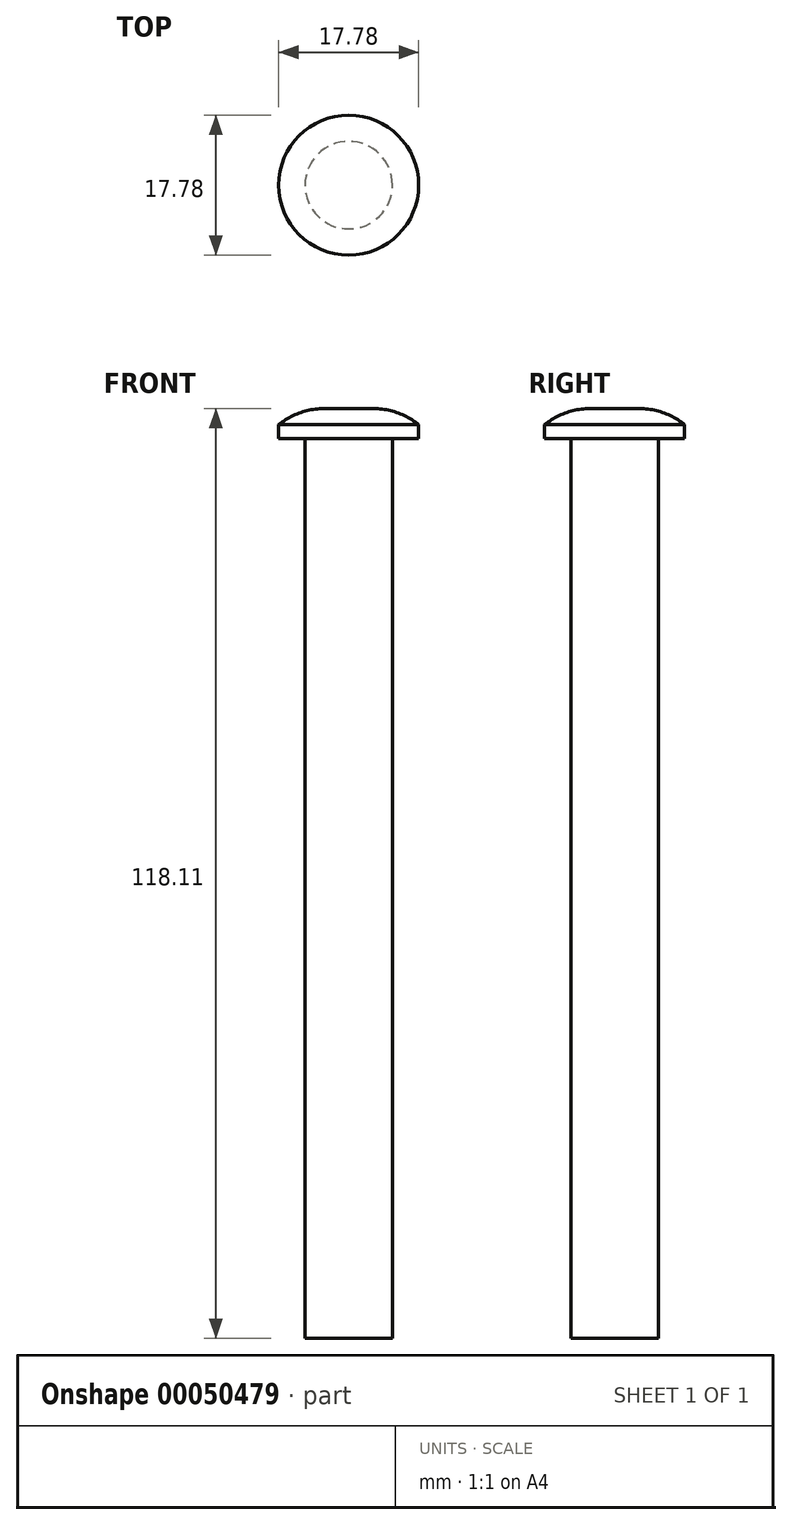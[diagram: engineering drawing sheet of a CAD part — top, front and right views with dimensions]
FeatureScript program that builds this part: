
annotation { "Feature Type Name" : "Feature", "Feature Type Description" : "" }
export const myFeature = defineFeature(function(context is Context, id is Id, definition is map)
    precondition{}
    {
        {
            var Q0;
            Q0=qCreatedBy(makeId("Top.planeOp"),FACE);
            var sketch = newSketch(context, id + "F0", { "sketchPlane" : qUnion([Q0])});
            skCircle(sketch, "E0", {"center": v(0, 0) * mm, "radius": 5.56 * mm});
            skSolve(sketch);
        }
        {
            var Q0;
            Q0 = qSketchRegion(id + "F0", true);
            extrude(context, id + "F1", {"entities" : qUnion([Q0]), "endBound" : BoundingType.SYMMETRIC, "depth" : 114.3 * mm});
        }
        {
            var Q0;
            Q0=qCreatedBy(makeId("Front.planeOp"),FACE);
            var sketch = newSketch(context, id + "F2", { "sketchPlane" : qUnion([Q0])});
            skLineSegment(sketch, "E1", {"start": v(5.56, 57.15) * mm, "end": v(8.9, 57.15) * mm});
            skLineSegment(sketch, "E2", {"start": v(8.9, 57.15) * mm, "end": v(8.9, 58.93) * mm});
            skLineSegment(sketch, "E3", {"start": v(0, 57.15) * mm, "end": v(0, 60.96) * mm});
            skPoint(sketch, "E3.endSnap0", {"position": v(0, 57.15) * mm});
            skLineSegment(sketch, "E4", {"start": v(0, 60.96) * mm, "end": v(3.18, 60.96) * mm});
            skPoint(sketch, "E5.orphan", {"position": v(-5.56, 57.15) * mm});
            skLineSegment(sketch, "E6", {"start": v(0, 60.96) * mm, "end": v(0, 71.12) * mm, "construction": true});
            skArc(sketch, "E7", {"start": v(8.9, 58.93) * mm, "mid": v(6.2, 60.44) * mm, "end": v(3.18, 60.96) * mm});
            skLineSegment(sketch, "E8", {"start": v(0, 57.15) * mm, "end": v(5.56, 57.15) * mm});
            skSolve(sketch);
        }
        {
            var Q0;
            Q0 = qSketchRegion(id + "F2", true);
            var Q1;
            Q1=sQuery(id+"F2.wireOp",EDGE,"E6");
            revolve(context, id + "F3", {"operationType" : NewBodyOperationType.ADD, "entities" : qUnion([Q0]), "axis" : qUnion([Q1]), "revolveType" : RevolveType.FULL});
        }
    });
